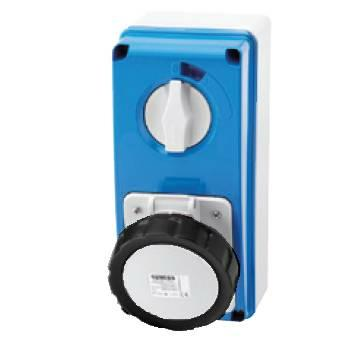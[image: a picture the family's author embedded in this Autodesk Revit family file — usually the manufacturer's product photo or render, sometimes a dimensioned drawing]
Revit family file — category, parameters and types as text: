
# Revit family: Building-IEC309Connections-GEWISS-67IB-INTERLOCKED-SOCKET-OUTLETS_IP67_WITH_BOTTOM_FUS
name_source: partatom
category: Apparecchi elettrici
revit_build: Autodesk Revit 2016 (Build: 20161004_0715(x64)
units: mm (PartAtom-declared; Revit-internal decimal feet)

## family parameters
Condiviso = No
Host = Muro
Mantenere orientamento annotazione = Sì
Numero OmniClass = 23.80.50.14
Punto di calcolo locali = No
Quota connettore circolare = Usa diametro
Sempre verticale = Sì
Taglio con vuoti quando caricato = No
Tipo di parte = Normale
Titolo OmniClass = Plug Connectors

## types (23) — shared parameters
Altezza da terra = 1112 mm
Carico apparente = 0 VA
Catalogue = BUILDING
Catalogue Range = 67 IB
Classificazione carico = Altro
Electrocod = 2222
Frequency = 50/60 Hz
Fuse breacking capacity = > 50 kA
Glow Wire Test = 850 °C (IB socket) - 650 °C (bottom)
Glow wire test: = 850 °C (IB socket) - 650 °C (bottom)
IDF = f9d0bb66-5de6-40f3-bd54-3f6ca6852506
IDT = 3a2f285e-e7b7-489c-a67e-4c14f132aefb
IP degree = IP67
Immagine tipo = GW66230N.jpg
Numero poli = 3
Operating temperature: = -25 +40 °C
Potenza = 400 V
Presa = GW - ROSSO
Produttore = GEWISS S.p.A.
Protection = Fuse-holder base (CBF)
Rated frequency (Hz) = 50/60 Hz
Rated impulse withstand voltage = 4KV
Rated insulation voltage (Ui) = 500V
Rated short-circuit current (Icc) = 10KA
SEO = Socket outlet
Shock resistance = IK08
Struttura = GEWISS - Grigio RAL - 7035
Struttura frontale = GEWISS -BLU
Technical sheet = https://www.gewiss.com
Thermo-pressure with ball = 125 °C (IB socket) - 80 °C (bottom)
Tipo Simbolo = PRESAINDPFUS : 3P
Type of fuse = Ã˜ 10.3x38 mm
Typology = Vertical
URL = https://www.gewiss.com
Version file RFA = 18.0
Vetro = GEWISS - vetro
With back-mounting box = Yes
Working temperature = -25 ÷ +40 °C

## per-type parameters (varying)
| type | Colour | Colour: | Descrizione | EAN code | IB socket outlet rated current (In) | Modello | No. of poles | Number of poles | Rated current (A) | Rated current (In) | Rated voltage | Rated voltage: | Reference h | Weight | Weight (kg) |
| GW66244N - 32A 3P+N+E 500V V.INT.SOCK.O.W.B.7H CBF | Black | Black | 32A 3P+N+E 500V V.INT.SOCK.O.W.B.7H CBF | 8011564741515 | 28A | GW66244N | 3P+N+E | 3P+N+E | 32 | 32 | 480 - 500 V | 480 - 500 V | 7 | Max. 1.1 Kg | Max. 1.1 Kg |
| GW66234N - 32A 2P+E 110V V.INT.SOCK.O.W.B.4H CBF | Yellow | Yellow | 32A 2P+E 110V V.INT.SOCK.O.W.B.4H CBF | 8011564741430 | 32A | GW66234N | 2P+E | 2P+E | 32 | 32 | 100 - 130 V | 100 - 130 V | 4 | Max. 1.1 Kg | Max. 1.1 Kg |
| GW66226N - 16A 2P+E 230V V.INT.SOCK.O.W.B.6H CBF | Blue | Blue | 16A 2P+E 230V V.INT.SOCK.O.W.B.6H CBF | 8011564741362 | 16A | GW66226N | 2P+E | 2P+E | 16 | 16 | 200 - 250 V | 200 - 250 V | 6 | Max. 1.0 Kg | Max. 1.0 Kg |
| GW66237N - 32A 2P+E 230V V.INT.SOCK.O.W.B.6H CBF | Blue | Blue | 32A 2P+E 230V V.INT.SOCK.O.W.B.6H CBF | 8011564742550 | 32A | GW66237N | 2P+E | 2P+E | 32 | 32 | 200 - 250 V | 200 - 250 V | 6 | Max. 1.1 Kg | Max. 1.1 Kg |
| GW66235N - 32A 3P+E 110V V.INT.SOCK.O.W.B.4H CBF | Yellow | Yellow | 32A 3P+E 110V V.INT.SOCK.O.W.B.4H CBF | 8011564741447 | 28A | GW66235N | 3P+E | 3P+E | 32 | 32 | 100 - 130 V | 100 - 130 V | 4 | Max. 1.1 Kg | Max. 1.1 Kg |
| GW66240N - 32A 2P+E 400V V.INT.SOCK.O.W.B.9H CBF | Red | Red | 32A 2P+E 400V V.INT.SOCK.O.W.B.9H CBF | 8011564741485 | 32A | GW66240N | 2P+E | 2P+E | 32 | 32 | 380 - 415 V | 380 - 415 V | 9 | Max. 1.1 Kg | Max. 1.1 Kg |
| GW66223N - 16A 2P+E 110V V.INT.SOCK.O.W.B.4H CBF | Yellow | Yellow | 16A 2P+E 110V V.INT.SOCK.O.W.B.4H CBF | 8011564741331 | 16A | GW66223N | 2P+E | 2P+E | 16 | 16 | 100 - 130 V | 100 - 130 V | 4 | Max. 1.0 Kg | Max. 1.0 Kg |
| GW66227N - 16A 3P+E 230V V.INT.SOCK.O.W.B.9H CBF | Blue | Blue | 16A 3P+E 230V V.INT.SOCK.O.W.B.9H CBF | 8011564741379 | 16A | GW66227N | 3P+E | 3P+E | 16 | 16 | 200 - 250 V | 200 - 250 V | 9 | Max. 1.0 Kg | Max. 1.0 Kg |
| GW66238N - 32A 3P+E 230V V.INT.SOCK.O.W.B.9H CBF | Blue | Blue | 32A 3P+E 230V V.INT.SOCK.O.W.B.9H CBF | 8011564741461 | 28A | GW66238N | 3P+E | 3P+E | 32 | 32 | 200 - 250 V | 200 - 250 V | 9 | Max. 1.1 Kg | Max. 1.1 Kg |
| GW66243N - 32A 3P+E 500V V.INT.SOCK.O.W.B.7H CBF | Black | Black | 32A 3P+E 500V V.INT.SOCK.O.W.B.7H CBF | 8011564741508 | 28A | GW66243N | 3P+E | 3P+E | 32 | 32 | 480 - 500 V | 480 - 500 V | 7 | Max. 1.1 Kg | Max. 1.1 Kg |
| GW66229N - 16A 2P+E 400V V.INT.SOCK.O.W.B.9H CBF | Red | Red | 16A 2P+E 400V V.INT.SOCK.O.W.B.9H CBF | 8011564741393 | 16A | GW66229N | 2P+E | 2P+E | 16 | 16 | 380 - 415 V | 380 - 415 V | 9 | Max. 1.0 Kg | Max. 1.0 Kg |
| GW66233N - 16A 3P+N+E 500V V.INT.SOCK.O.W.B.7H CBF | Black | Black | 16A 3P+N+E 500V V.INT.SOCK.O.W.B.7H CBF | 8011564741423 | 16A | GW66233N | 3P+N+E | 3P+N+E | 16 | 16 | 480 - 500 V | 480 - 500 V | 7 | Max. 1.0 Kg | Max. 1.0 Kg |
| GW66236N - 32A 3P+N+E 110V V.INT.SOCK.O.W.B.4H CBF | Yellow | Yellow | 32A 3P+N+E 110V V.INT.SOCK.O.W.B.4H CBF | 8011564741454 | 28A | GW66236N | 3P+N+E | 3P+N+E | 32 | 32 | 100 - 130 V | 100 - 130 V | 4 | Max. 1.1 Kg | Max. 1.1 Kg |
| GW66242N - 32A 3P+N+E 400V V.INT.SOCK.O.W.B.6H CBF | Red | Red | 32A 3P+N+E 400V V.INT.SOCK.O.W.B.6H CBF | 8011564742567 | 28A | GW66242N | 3P+N+E | 3P+N+E | 32 | 32 | 380 - 415 V | 380 - 415 V | 6 | Max. 1.1 Kg | Max. 1.1 Kg |
| GW66232N - 16A 3P+E 500V V.INT.SOCK.O.W.B.7H CBF | Black | Black | 16A 3P+E 500V V.INT.SOCK.O.W.B.7H CBF | 8011564741416 | 16A | GW66232N | 3P+E | 3P+E | 16 | 16 | 480 - 500 V | 480 - 500 V | 7 | Max. 1.0 Kg | Max. 1.0 Kg |
| GW66241N - 32A 3P+E 400V V.INT.SOCK.O.W.B.6H CBF | Red | Red | 32A 3P+E 400V V.INT.SOCK.O.W.B.6H CBF | 8011564741492 | 28A | GW66241N | 3P+E | 3P+E | 32 | 32 | 380 - 415 V | 380 - 415 V | 6 | Max. 1.1 Kg | Max. 1.1 Kg |
| GW66239N - 32A 3P+N+E 230V V.INT.SOCK.O.W.B.9H CBF | Blue | Blue | 32A 3P+N+E 230V V.INT.SOCK.O.W.B.9H CBF | 8011564741478 | 28A | GW66239N | 3P+N+E | 3P+N+E | 32 | 32 | 200 - 250 V | 200 - 250 V | 9 | Max. 1.1 Kg | Max. 1.1 Kg |
| GW66258N - 32A 3P+E 380V V.INT.SOCK.O.W.B.3H CBF | Red | Red | 32A 3P+E 380V V.INT.SOCK.O.W.B.3H CBF | 8011564741539 | 28A | GW66258N | 3P+E | 3P+E | 32 | 32 | 380 - 440 V | 380 - 440 V | 3 | Max. 1.1 Kg | Max. 1.1 Kg |
| GW66230N - 16A 3P+E 400V V.INT.SOCK.O.W.B.6H CBF | Red | Red | 16A 3P+E 400V V.INT.SOCK.O.W.B.6H CBF | 8011564741409 | 16A | GW66230N | 3P+E | 3P+E | 16 | 16 | 380 - 415 V | 380 - 415 V | 6 | Max. 1.0 Kg | Max. 1.0 Kg |
| GW66225N - 16A 3P+N+E 110V V.INT.SOCK.O.W.B.4H CBF | Yellow | Yellow | 16A 3P+N+E 110V V.INT.SOCK.O.W.B.4H CBF | 8011564741355 | 16A | GW66225N | 3P+N+E | 3P+N+E | 16 | 16 | 100 - 130 V | 100 - 130 V | 4 | Max. 1.0 Kg | Max. 1.0 Kg |
| GW66228N - 16A 3P+N+E 230V V.INT.SOCK.O.W.B.9H CBF | Blue | Blue | 16A 3P+N+E 230V V.INT.SOCK.O.W.B.9H CBF | 8011564741386 | 16A | GW66228N | 3P+N+E | 3P+N+E | 16 | 16 | 200 - 250 V | 200 - 250 V | 9 | Max. 1.0 Kg | Max. 1.0 Kg |
| GW66224N - 16A 3P+E 110V V.INT.SOCK.O.W.B.4H CBF | Yellow | Yellow | 16A 3P+E 110V V.INT.SOCK.O.W.B.4H CBF | 8011564741348 | 16A | GW66224N | 3P+E | 3P+E | 16 | 16 | 100 - 130 V | 100 - 130 V | 4 | Max. 1.0 Kg | Max. 1.0 Kg |
| GW66231N - 16A 3P+N+E 400V V.INT.SOCK.O.W.B.6H CBF | Red | Red | 16A 3P+N+E 400V V.INT.SOCK.O.W.B.6H CBF | 8011564742543 | 16A | GW66231N | 3P+N+E | 3P+N+E | 16 | 16 | 380 - 415 V | 380 - 415 V | 6 | Max. 1.0 Kg | Max. 1.0 Kg |

## geometry (parser evidence)
native form markers: Blend x4, Sweep x1
no freeform markers — native parametric forms only
